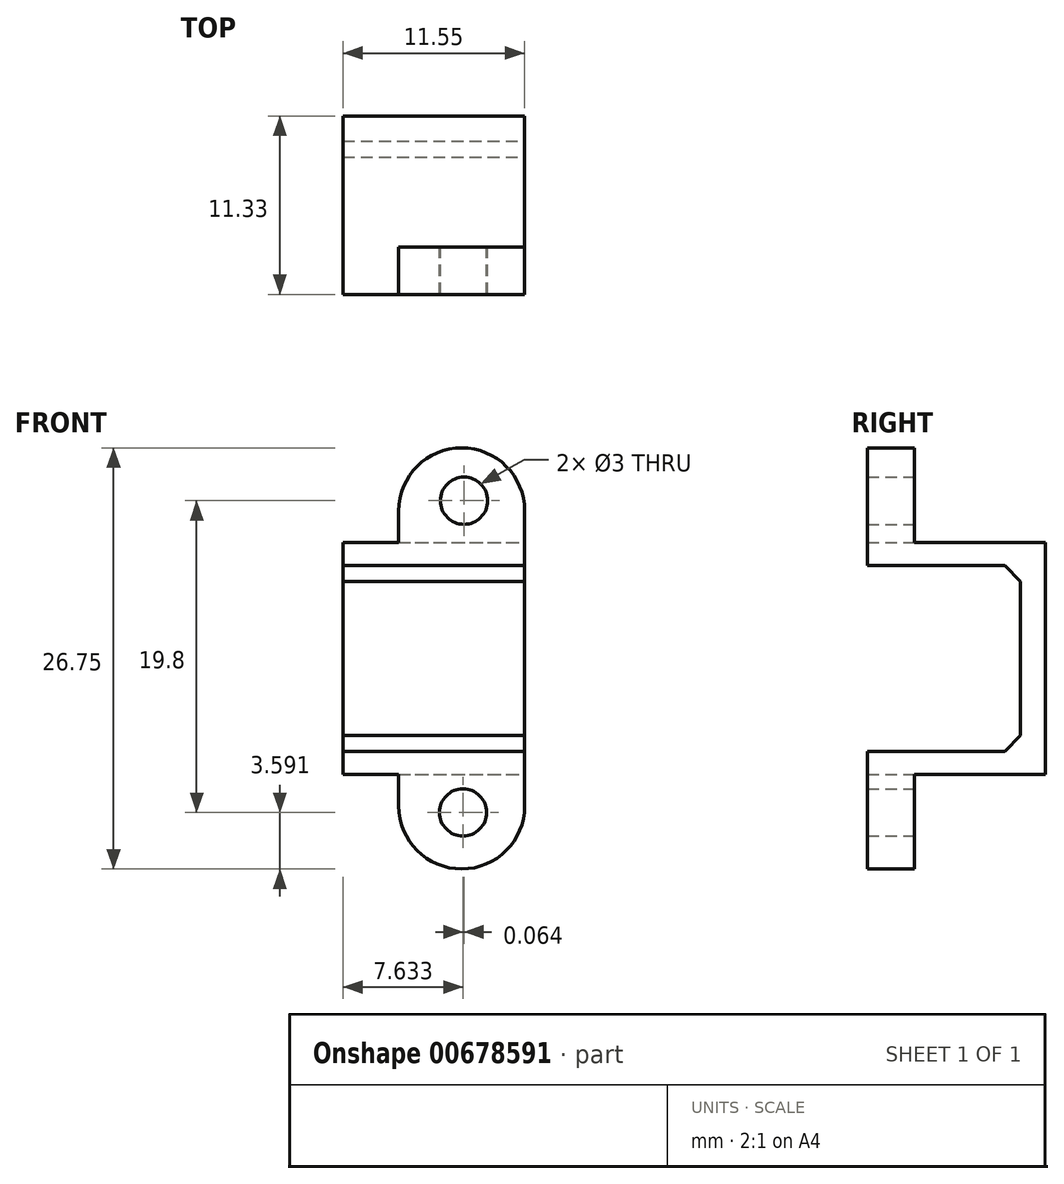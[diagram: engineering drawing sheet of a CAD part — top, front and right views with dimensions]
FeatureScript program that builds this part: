
annotation { "Feature Type Name" : "Feature", "Feature Type Description" : "" }
export const myFeature = defineFeature(function(context is Context, id is Id, definition is map)
    precondition{}
    {
        {
            var Q0;
            Q0=qCreatedBy(makeId("Front.planeOp"),FACE);
            var sketch = newSketch(context, id + "F0", { "sketchPlane" : qUnion([Q0])});
            skLineSegment(sketch, "E0.bottom", {"start": v(0, 0) * mm, "end": v(11.55, 0) * mm});
            skLineSegment(sketch, "E0.top", {"start": v(0, 14.75) * mm, "end": v(11.55, 14.75) * mm});
            skLineSegment(sketch, "E0.left", {"start": v(0, 0) * mm, "end": v(0, 14.75) * mm});
            skLineSegment(sketch, "E0.right", {"start": v(11.55, 0) * mm, "end": v(11.55, 14.75) * mm});
            skLineSegment(sketch, "E1", {"start": v(0, 14.75) * mm, "end": v(0, 13.27) * mm});
            skLineSegment(sketch, "E2", {"start": v(0, 13.27) * mm, "end": v(11.55, 13.27) * mm});
            skLineSegment(sketch, "E3", {"start": v(0, 0) * mm, "end": v(0, 1.48) * mm});
            skLineSegment(sketch, "E4", {"start": v(0, 1.48) * mm, "end": v(11.55, 1.48) * mm});
            skLineSegment(sketch, "E5", {"start": v(11.55, 1.48) * mm, "end": v(11.55, 0) * mm});
            skSolve(sketch);
        }
        {
            var Q0;
            Q0=makeQuery(id+"F0.imprint","IMPRINT",FACE,{"disambiguationData":[TD([[makeQuery(id+"F0.imprint","IMPRINT",EDGE,{"derivedFrom":sQuery(id+"F0.wireOp",EDGE,"E0.bottom")}),1.0]])]});
            var Q1;
            {var subQ0=sQuery(id+"F0.wireOp",EDGE,"E0.top");Q1=makeQuery(id+"F0.imprint","IMPRINT",FACE,{"disambiguationData":[TD([[makeQuery(id+"F0.imprint","IMPRINT",EDGE,{"derivedFrom":subQ0}),-1.0]])]});}
            var Q2;
            Q2=makeQuery(id+"F0.imprint","IMPRINT",FACE,{"disambiguationData":[TD([[makeQuery(id+"F0.imprint","IMPRINT",EDGE,{"derivedFrom":sQuery(id+"F0.wireOp",EDGE,"E0.left")}),-1.0]])]});
            extrude(context, id + "F1", {"entities" : qUnion([Q0, Q1, Q2]), "depth" : 11.33 * mm, "offsetDistance" : 25 * mm});
        }
        {
            var Q0;
            Q0=makeQuery(id+"F1.opExtrude","CAP_FACE",FACE,{"disambiguationData":[OSD([sQuery(id+"F0.wireOp",EDGE,"E0.bottom"),sQuery(id+"F0.wireOp",EDGE,"E0.top"),sQuery(id+"F0.wireOp",EDGE,"E0.left"),sQuery(id+"F0.wireOp",EDGE,"E0.right"),sQuery(id+"F0.wireOp",EDGE,"E1"),sQuery(id+"F0.wireOp",EDGE,"E3"),sQuery(id+"F0.wireOp",EDGE,"E5")])],"isStart":false});
            var sketch = newSketch(context, id + "F2", { "sketchPlane" : qUnion([Q0])});
            skLineSegment(sketch, "E6", {"start": v(0, 14.75) * mm, "end": v(0, 13.27) * mm});
            skLineSegment(sketch, "E7", {"start": v(0, 13.27) * mm, "end": v(11.55, 13.27) * mm});
            skLineSegment(sketch, "E8", {"start": v(0, 0) * mm, "end": v(0, 1.48) * mm});
            skLineSegment(sketch, "E9", {"start": v(0, 1.48) * mm, "end": v(11.55, 1.48) * mm});
            skLineSegment(sketch, "E10", {"start": v(0, 13.27) * mm, "end": v(0, 1.48) * mm});
            skLineSegment(sketch, "E11", {"start": v(11.55, 13.27) * mm, "end": v(11.55, 1.48) * mm});
            skSolve(sketch);
        }
        {
            var Q0;
            Q0=makeQuery(id+"F2.imprint","IMPRINT",FACE,{"disambiguationData":[TD([[makeQuery(id+"F2.imprint","IMPRINT",EDGE,{"derivedFrom":sQuery(id+"F2.wireOp",EDGE,"E7")}),-1.0]])]});
            extrude(context, id + "F3", {"entities" : qUnion([Q0]), "operationType" : NewBodyOperationType.REMOVE, "oppositeDirection" : true, "depth" : 9.73 * mm, "offsetDistance" : 25 * mm});
        }
        {
            var Q0;
            Q0=makeQuery(id+"F1.opExtrude","SWEPT_FACE",FACE,{"disambiguationData":[OSD([sQuery(id+"F0.wireOp",EDGE,"E0.right"),sQuery(id+"F0.wireOp",EDGE,"E5")])]});
            var sketch = newSketch(context, id + "F4", { "sketchPlane" : qUnion([Q0])});
            skLineSegment(sketch, "E12", {"start": v(-11.33, 14.75) * mm, "end": v(-11.33, 20.75) * mm});
            skLineSegment(sketch, "E13", {"start": v(-11.33, 20.75) * mm, "end": v(-8.33, 20.75) * mm});
            skLineSegment(sketch, "E14", {"start": v(-8.33, 20.75) * mm, "end": v(-8.33, 14.75) * mm});
            skLineSegment(sketch, "E15", {"start": v(-8.33, 14.75) * mm, "end": v(-11.33, 14.75) * mm});
            skSolve(sketch);
        }
        {
            var Q0;
            Q0=makeQuery(id+"F4.imprint","IMPRINT",FACE,{"disambiguationData":[TD([[makeQuery(id+"F4.imprint","IMPRINT",EDGE,{"derivedFrom":sQuery(id+"F4.wireOp",EDGE,"E12")}),-1.0]])]});
            var Q1;
            {var subQ5=sQuery(id+"F4.wireOp",EDGE,"E15");Q1=makeQuery(id+"F4.imprint","IMPRINT",FACE,{"disambiguationData":[TD([[makeQuery(id+"F4.imprint","IMPRINT",EDGE,{"derivedFrom":subQ5}),-1.0]])]});}
            extrude(context, id + "F5", {"entities" : qUnion([Q0, Q1]), "operationType" : NewBodyOperationType.ADD, "oppositeDirection" : true, "depth" : 8 * mm, "offsetDistance" : 25 * mm});
        }
        {
            var Q0;
            {var subQ0=sQuery(id+"F0.wireOp",EDGE,"E5");var subQ1=sQuery(id+"F0.wireOp",EDGE,"E0.right");Q0=makeQuery(id+"F5.boolean.opBoolean","MERGE",FACE,{"derivedFrom":[makeQuery(id+"F1.opExtrude","SWEPT_FACE",FACE,{"disambiguationData":[OSD([subQ1,subQ0])]}),makeQuery(id+"F5.opExtrude","CAP_FACE",FACE,{"disambiguationData":[OSD([sQuery(id+"F0.wireOp",EDGE,"E0.bottom"),sQuery(id+"F0.wireOp",EDGE,"E0.top"),subQ1,subQ0,sQuery(id+"F2.wireOp",EDGE,"E7"),sQuery(id+"F2.wireOp",EDGE,"E9"),sQuery(id+"F2.wireOp",EDGE,"E11"),sQuery(id+"F4.wireOp",EDGE,"E12"),sQuery(id+"F4.wireOp",EDGE,"E13"),sQuery(id+"F4.wireOp",EDGE,"E14")])],"isStart":true})]});}
            var sketch = newSketch(context, id + "F6", { "sketchPlane" : qUnion([Q0])});
            skLineSegment(sketch, "E16", {"start": v(-11.33, 0) * mm, "end": v(-11.33, -6) * mm});
            skLineSegment(sketch, "E17", {"start": v(-11.33, -6) * mm, "end": v(-8.33, -6) * mm});
            skLineSegment(sketch, "E18", {"start": v(-8.33, -6) * mm, "end": v(-8.33, 0) * mm});
            skLineSegment(sketch, "E19", {"start": v(-8.33, 0) * mm, "end": v(-11.33, 0) * mm});
            skSolve(sketch);
        }
        {
            var Q0;
            Q0=makeQuery(id+"F6.imprint","IMPRINT",FACE,{"disambiguationData":[TD([[makeQuery(id+"F6.imprint","IMPRINT",EDGE,{"derivedFrom":sQuery(id+"F6.wireOp",EDGE,"E16")}),1.0]])]});
            extrude(context, id + "F7", {"entities" : qUnion([Q0]), "operationType" : NewBodyOperationType.ADD, "oppositeDirection" : true, "depth" : 8 * mm, "offsetDistance" : 25 * mm});
        }
        {
            var Q0;
            Q0=makeQuery(id+"F5.opExtrude","CAP_EDGE",EDGE,{"disambiguationData":[OSD([sQuery(id+"F4.wireOp",EDGE,"E13")])],"isStart":true});
            fillet(context, id + "F8", {"entities" : qUnion([Q0]), "radius" : 4 * mm, "tangentPropagation" : true, "allowEdgeOverflow" : false});
        }
        {
            var Q0;
            Q0=makeQuery(id+"F5.opExtrude","CAP_EDGE",EDGE,{"disambiguationData":[OSD([sQuery(id+"F4.wireOp",EDGE,"E13")])],"isStart":false});
            fillet(context, id + "F9", {"entities" : qUnion([Q0]), "radius" : 4 * mm, "tangentPropagation" : true, "allowEdgeOverflow" : false});
        }
        {
            var Q0;
            Q0=makeQuery(id+"F7.opExtrude","CAP_EDGE",EDGE,{"disambiguationData":[OSD([sQuery(id+"F6.wireOp",EDGE,"E17")])],"isStart":true});
            fillet(context, id + "F10", {"entities" : qUnion([Q0]), "radius" : 4 * mm, "tangentPropagation" : true, "allowEdgeOverflow" : false});
        }
        {
            var Q0;
            Q0=makeQuery(id+"F7.opExtrude","CAP_EDGE",EDGE,{"disambiguationData":[OSD([sQuery(id+"F6.wireOp",EDGE,"E17")])],"isStart":false});
            fillet(context, id + "F11", {"entities" : qUnion([Q0]), "radius" : 4 * mm, "tangentPropagation" : true, "allowEdgeOverflow" : false});
        }
        {
            var Q0;
            Q0=makeQuery(id+"F7.opExtrude","SWEPT_FACE",FACE,{"disambiguationData":[OSD([sQuery(id+"F6.wireOp",EDGE,"E18")])]});
            var sketch = newSketch(context, id + "F12", { "sketchPlane" : qUnion([Q0])});
            skCircle(sketch, "E20", {"center": v(-7.63, -2.4) * mm, "radius": 1.5 * mm});
            skSolve(sketch);
        }
        {
            var Q0;
            Q0=qSketchRegion(id+"F12",true);
            extrude(context, id + "F13", {"entities" : qUnion([Q0]), "operationType" : NewBodyOperationType.REMOVE, "oppositeDirection" : true, "depth" : 25 * mm, "offsetDistance" : 25 * mm});
        }
        {
            var Q0;
            Q0=makeQuery(id+"F5.opExtrude","SWEPT_FACE",FACE,{"disambiguationData":[OSD([sQuery(id+"F4.wireOp",EDGE,"E14")])]});
            var sketch = newSketch(context, id + "F14", { "sketchPlane" : qUnion([Q0])});
            skCircle(sketch, "E21", {"center": v(-7.7, 17.4) * mm, "radius": 1.5 * mm});
            skSolve(sketch);
        }
        {
            var Q0;
            Q0=qSketchRegion(id+"F14",true);
            extrude(context, id + "F15", {"entities" : qUnion([Q0]), "operationType" : NewBodyOperationType.REMOVE, "oppositeDirection" : true, "depth" : 25 * mm, "offsetDistance" : 25 * mm});
        }
        {
            var Q0;
            Q0=makeQuery(id+"F3.boolean.opBoolean","COPY",EDGE,{"derivedFrom":makeQuery(id+"F3.opExtrude","CAP_EDGE",EDGE,{"disambiguationData":[OSD([sQuery(id+"F2.wireOp",EDGE,"E7")])],"isStart":false})});
            chamfer(context, id + "F16", {"entities" : qUnion([Q0]), "width" : 1 * mm, "tangentPropagation" : true});
        }
        {
            var Q0;
            Q0=makeQuery(id+"F3.boolean.opBoolean","COPY",EDGE,{"derivedFrom":makeQuery(id+"F3.opExtrude","CAP_EDGE",EDGE,{"disambiguationData":[OSD([sQuery(id+"F2.wireOp",EDGE,"E9")])],"isStart":false})});
            chamfer(context, id + "F17", {"entities" : qUnion([Q0]), "width" : 1 * mm, "tangentPropagation" : true});
        }
    });
